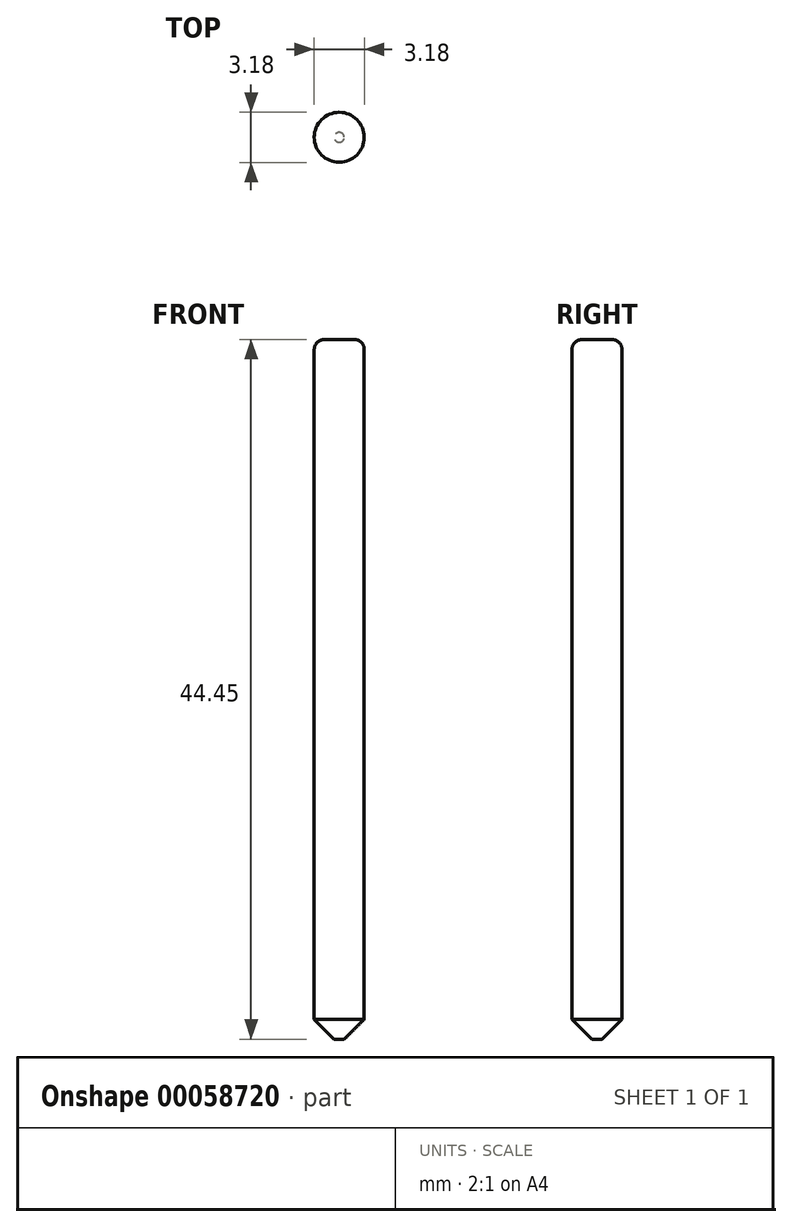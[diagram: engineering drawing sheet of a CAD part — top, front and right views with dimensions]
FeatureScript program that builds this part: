
annotation { "Feature Type Name" : "Feature", "Feature Type Description" : "" }
export const myFeature = defineFeature(function(context is Context, id is Id, definition is map)
    precondition{}
    {
        {
            var Q0;
            Q0=qCreatedBy(makeId("Top.planeOp"),FACE);
            var sketch = newSketch(context, id + "F0", { "sketchPlane" : qUnion([Q0])});
            skCircle(sketch, "E0", {"center": v(0, 0) * mm, "radius": 1.59 * mm});
            skSolve(sketch);
        }
        {
            var Q0;
            Q0=makeQuery(id+"F0.imprint","IMPRINT",FACE,{"disambiguationData":[TD([[makeQuery(id+"F0.imprint","IMPRINT",EDGE,{"derivedFrom":sQuery(id+"F0.wireOp",EDGE,"E0")}),1.0]])]});
            extrude(context, id + "F1", {"entities" : qUnion([Q0]), "depth" : 44.45 * mm});
        }
        {
            var Q0;
            Q0=makeQuery(id+"F1.opExtrude","CAP_EDGE",EDGE,{"disambiguationData":[OSD([sQuery(id+"F0.wireOp",EDGE,"E0")])],"isStart":false});
            fillet(context, id + "F2", {"entities" : qUnion([Q0]), "radius" : 0.64 * mm, "tangentPropagation" : true, "allowEdgeOverflow" : false});
        }
        {
            var Q0;
            Q0=makeQuery(id+"F1.opExtrude","CAP_EDGE",EDGE,{"disambiguationData":[OSD([sQuery(id+"F0.wireOp",EDGE,"E0")])],"isStart":true});
            chamfer(context, id + "F3", {"entities" : qUnion([Q0]), "width" : 1.27 * mm, "tangentPropagation" : true});
        }
    });
